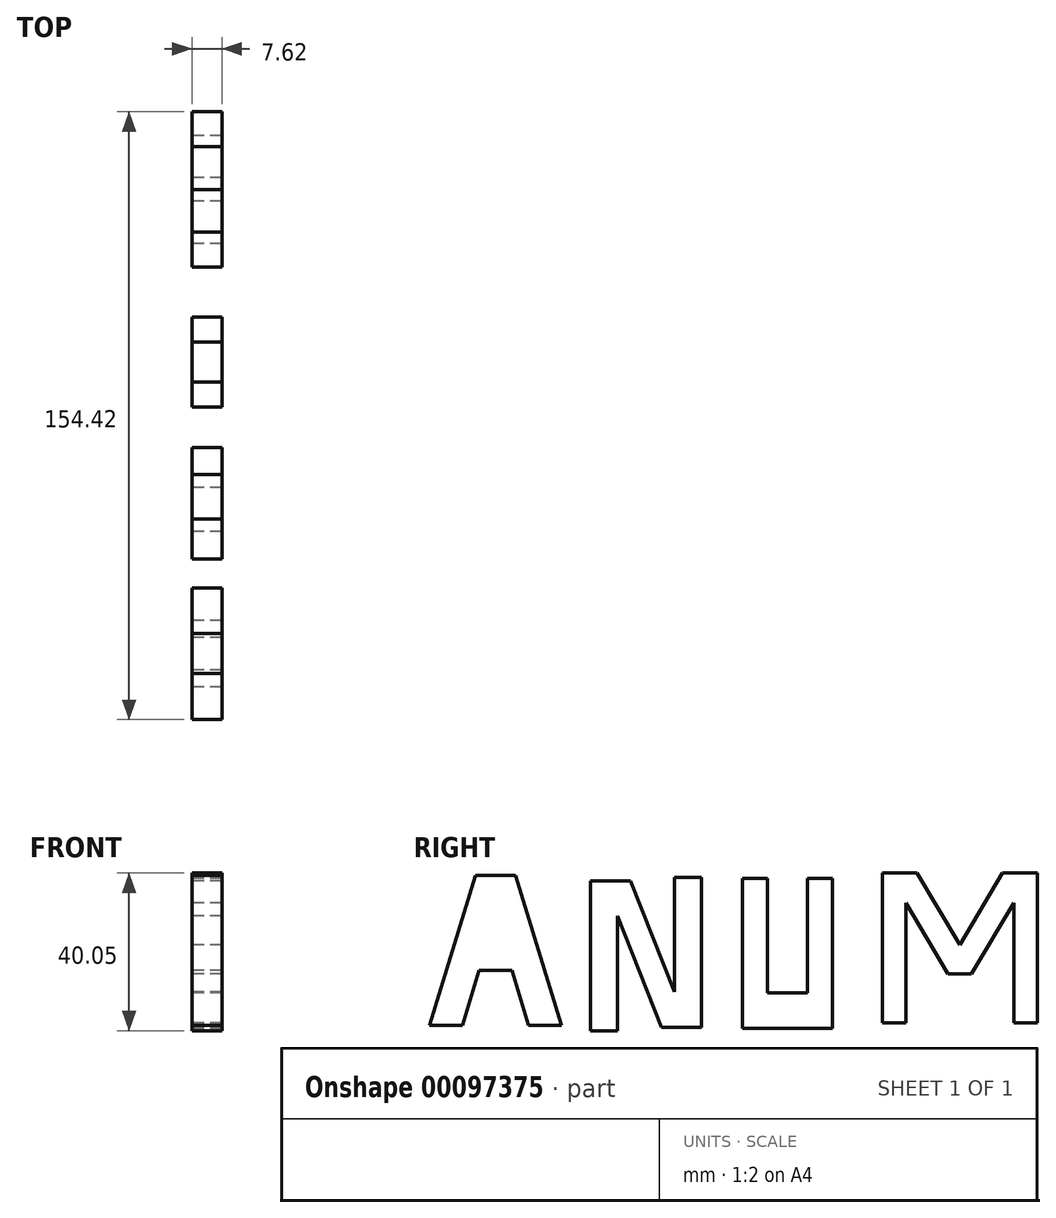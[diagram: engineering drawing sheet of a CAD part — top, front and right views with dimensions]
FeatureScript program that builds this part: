
annotation { "Feature Type Name" : "Feature", "Feature Type Description" : "" }
export const myFeature = defineFeature(function(context is Context, id is Id, definition is map)
    precondition{}
    {
        {
            var Q0;
            Q0=qCreatedBy(makeId("Right.planeOp"),FACE);
            var sketch = newSketch(context, id + "F0", { "sketchPlane" : qUnion([Q0])});
            skLineSegment(sketch, "E0", {"start": v(-75.16, -8.4) * mm, "end": v(-63.5, 29.7) * mm});
            skLineSegment(sketch, "E1", {"start": v(-63.5, 29.7) * mm, "end": v(-53.34, 29.7) * mm});
            skLineSegment(sketch, "E2", {"start": v(-53.34, 29.7) * mm, "end": v(-41.68, -8.4) * mm});
            skLineSegment(sketch, "E3", {"start": v(-41.68, -8.4) * mm, "end": v(-50, -8.4) * mm});
            skLineSegment(sketch, "E4", {"start": v(-50, -8.4) * mm, "end": v(-54.26, 5.49) * mm});
            skLineSegment(sketch, "E5", {"start": v(-54.26, 5.49) * mm, "end": v(-62.58, 5.49) * mm});
            skLineSegment(sketch, "E6", {"start": v(-62.58, 5.49) * mm, "end": v(-66.84, -8.4) * mm});
            skLineSegment(sketch, "E7", {"start": v(-66.84, -8.4) * mm, "end": v(-75.16, -8.4) * mm});
            skLineSegment(sketch, "E8", {"start": v(-34.33, -9.82) * mm, "end": v(-34.33, 28.28) * mm});
            skLineSegment(sketch, "E9", {"start": v(-34.33, 28.28) * mm, "end": v(-24.17, 28.28) * mm});
            skLineSegment(sketch, "E10", {"start": v(-24.17, 28.28) * mm, "end": v(-12.95, 0) * mm});
            skLineSegment(sketch, "E11", {"start": v(-12.95, 0) * mm, "end": v(-12.95, 29.14) * mm});
            skLineSegment(sketch, "E12", {"start": v(-12.95, 29.14) * mm, "end": v(-6.07, 29.14) * mm});
            skLineSegment(sketch, "E13", {"start": v(-6.07, 29.14) * mm, "end": v(-6.07, -8.96) * mm});
            skLineSegment(sketch, "E14", {"start": v(-6.07, -8.96) * mm, "end": v(-16.23, -8.96) * mm});
            skLineSegment(sketch, "E15", {"start": v(-16.23, -8.96) * mm, "end": v(-27.45, 19.32) * mm});
            skLineSegment(sketch, "E16", {"start": v(-27.45, 19.32) * mm, "end": v(-27.45, -9.82) * mm});
            skLineSegment(sketch, "E17", {"start": v(-27.45, -9.82) * mm, "end": v(-34.33, -9.82) * mm});
            skLineSegment(sketch, "E18", {"start": v(4.3, 28.88) * mm, "end": v(4.3, -9.22) * mm});
            skLineSegment(sketch, "E19", {"start": v(4.3, -9.22) * mm, "end": v(27.16, -9.22) * mm});
            skLineSegment(sketch, "E20", {"start": v(27.16, -9.22) * mm, "end": v(27.16, 28.88) * mm});
            skLineSegment(sketch, "E21", {"start": v(27.16, 28.88) * mm, "end": v(20.8, 28.88) * mm});
            skLineSegment(sketch, "E22", {"start": v(20.8, 28.88) * mm, "end": v(20.8, -0.23) * mm});
            skLineSegment(sketch, "E23", {"start": v(20.8, -0.23) * mm, "end": v(10.65, -0.23) * mm});
            skLineSegment(sketch, "E24", {"start": v(10.65, -0.23) * mm, "end": v(10.65, 28.88) * mm});
            skLineSegment(sketch, "E25", {"start": v(10.65, 28.88) * mm, "end": v(4.3, 28.88) * mm});
            skLineSegment(sketch, "E26", {"start": v(39.81, -7.87) * mm, "end": v(39.81, 30.23) * mm});
            skLineSegment(sketch, "E27", {"start": v(39.81, 30.23) * mm, "end": v(48.7, 30.23) * mm});
            skLineSegment(sketch, "E28", {"start": v(48.7, 30.23) * mm, "end": v(59.54, 11.99) * mm});
            skLineSegment(sketch, "E29", {"start": v(59.54, 11.99) * mm, "end": v(70.37, 30.23) * mm});
            skLineSegment(sketch, "E30", {"start": v(70.37, 30.23) * mm, "end": v(79.26, 30.23) * mm});
            skLineSegment(sketch, "E31", {"start": v(79.26, 30.23) * mm, "end": v(79.26, -7.87) * mm});
            skLineSegment(sketch, "E32", {"start": v(79.26, -7.87) * mm, "end": v(73.25, -7.87) * mm});
            skLineSegment(sketch, "E33", {"start": v(73.25, -7.87) * mm, "end": v(73.25, 22.64) * mm});
            skLineSegment(sketch, "E34", {"start": v(73.25, 22.64) * mm, "end": v(62.54, 4.61) * mm});
            skLineSegment(sketch, "E35", {"start": v(62.54, 4.61) * mm, "end": v(56.53, 4.61) * mm});
            skLineSegment(sketch, "E36", {"start": v(56.53, 4.61) * mm, "end": v(45.83, 22.64) * mm});
            skLineSegment(sketch, "E37", {"start": v(45.83, 22.64) * mm, "end": v(45.83, -7.87) * mm});
            skLineSegment(sketch, "E38", {"start": v(45.83, -7.87) * mm, "end": v(39.81, -7.87) * mm});
            skSolve(sketch);
        }
        {
            var Q0;
            Q0=makeQuery(id+"F0.imprint","IMPRINT",FACE,{"disambiguationData":[TD([[makeQuery(id+"F0.imprint","IMPRINT",EDGE,{"derivedFrom":sQuery(id+"F0.wireOp",EDGE,"E0")}),-1.0]])]});
            var Q1;
            Q1=makeQuery(id+"F0.imprint","IMPRINT",FACE,{"disambiguationData":[TD([[makeQuery(id+"F0.imprint","IMPRINT",EDGE,{"derivedFrom":sQuery(id+"F0.wireOp",EDGE,"E8")}),-1.0]])]});
            var Q2;
            Q2=makeQuery(id+"F0.imprint","IMPRINT",FACE,{"disambiguationData":[TD([[makeQuery(id+"F0.imprint","IMPRINT",EDGE,{"derivedFrom":sQuery(id+"F0.wireOp",EDGE,"E18")}),1.0]])]});
            var Q3;
            Q3=makeQuery(id+"F0.imprint","IMPRINT",FACE,{"disambiguationData":[TD([[makeQuery(id+"F0.imprint","IMPRINT",EDGE,{"derivedFrom":sQuery(id+"F0.wireOp",EDGE,"E26")}),-1.0]])]});
            extrude(context, id + "F1", {"entities" : qUnion([Q0, Q1, Q2, Q3]), "depth" : 7.62 * mm});
        }
    });
